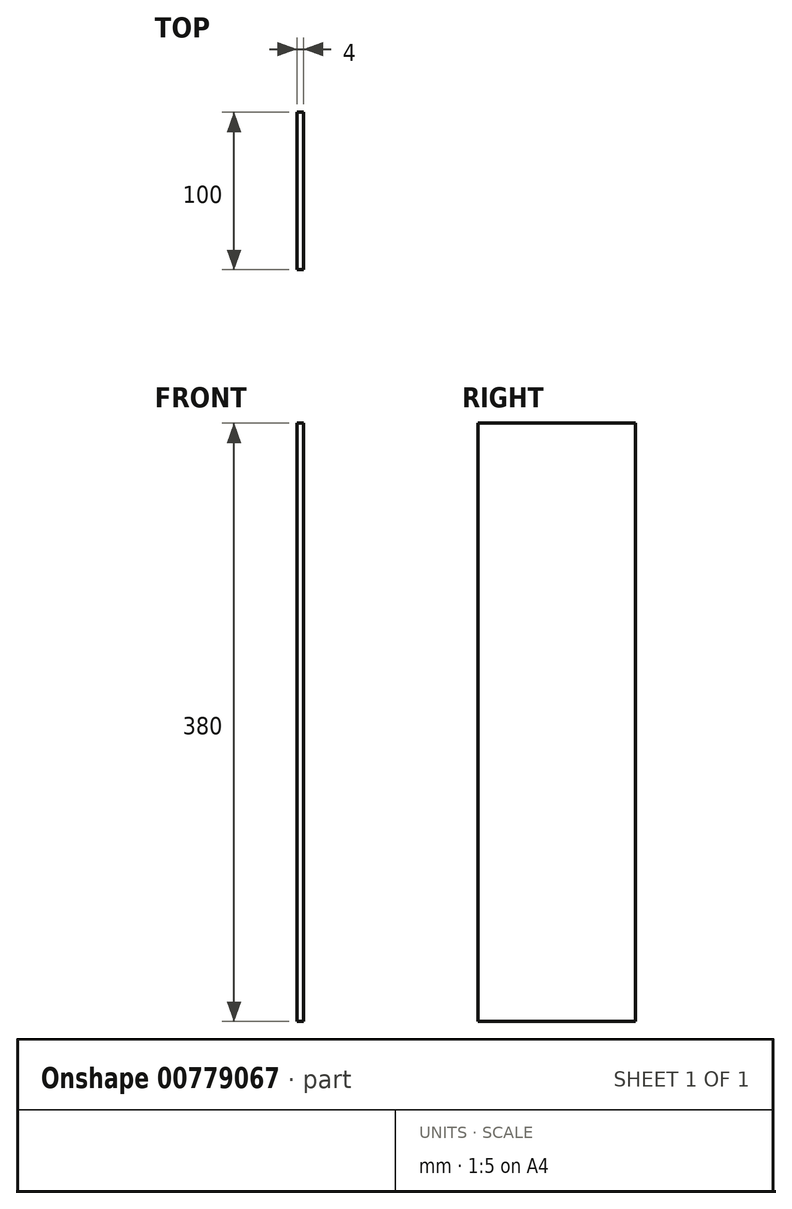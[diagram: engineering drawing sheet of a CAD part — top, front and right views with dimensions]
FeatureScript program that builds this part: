
annotation { "Feature Type Name" : "Feature", "Feature Type Description" : "" }
export const myFeature = defineFeature(function(context is Context, id is Id, definition is map)
    precondition{}
    {
        {
            var Q0;
            Q0=qCreatedBy(makeId("Right.planeOp"),FACE);
            var sketch = newSketch(context, id + "F0", { "sketchPlane" : qUnion([Q0])});
            skLineSegment(sketch, "E0.bottom", {"start": v(-50, 190) * mm, "end": v(50, 190) * mm});
            skLineSegment(sketch, "E0.top", {"start": v(-50, -190) * mm, "end": v(50, -190) * mm});
            skLineSegment(sketch, "E0.left", {"start": v(-50, 190) * mm, "end": v(-50, -190) * mm});
            skLineSegment(sketch, "E0.right", {"start": v(50, 190) * mm, "end": v(50, -190) * mm});
            skPoint(sketch, "E0.middle", {"position": v(0, 0) * mm});
            skSolve(sketch);
        }
        {
            var Q0;
            Q0=makeQuery(id+"F0.imprint","IMPRINT",FACE,{"disambiguationData":[TD([[makeQuery(id+"F0.imprint","IMPRINT",EDGE,{"derivedFrom":sQuery(id+"F0.wireOp",EDGE,"E0.bottom")}),-1.0]])]});
            extrude(context, id + "F1", {"entities" : qUnion([Q0]), "depth" : 4 * mm, "offsetDistance" : 25 * mm});
        }
    });
